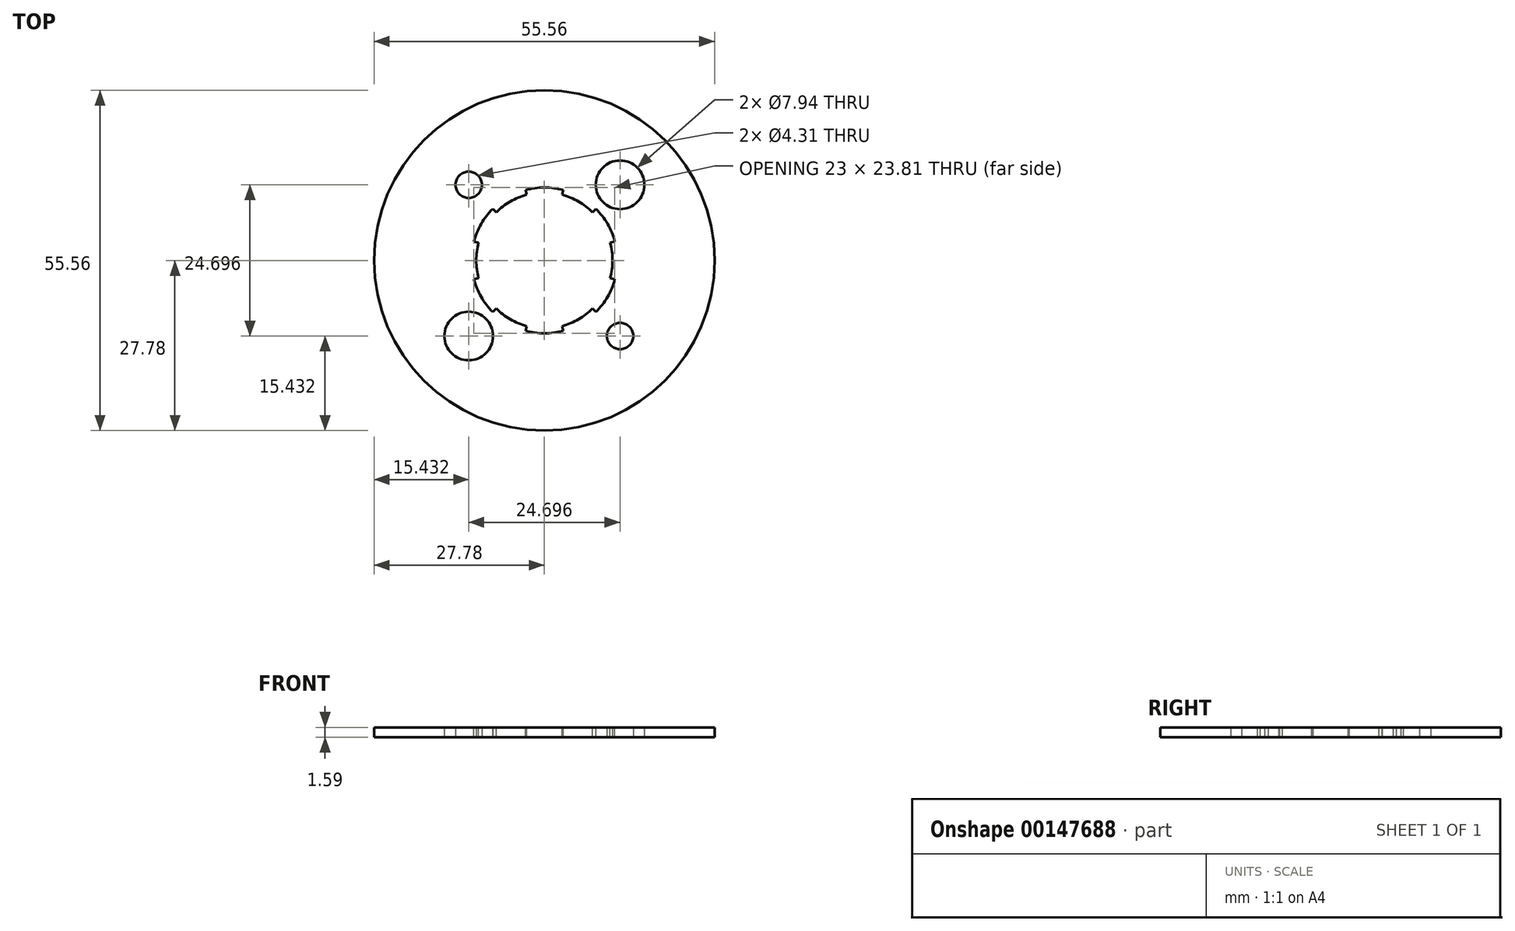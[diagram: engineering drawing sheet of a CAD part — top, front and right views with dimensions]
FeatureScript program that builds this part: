
annotation { "Feature Type Name" : "Feature", "Feature Type Description" : "" }
export const myFeature = defineFeature(function(context is Context, id is Id, definition is map)
    precondition{}
    {
        {
            var Q0;
            Q0=qCreatedBy(makeId("Top.planeOp"),FACE);
            var sketch = newSketch(context, id + "F0", { "sketchPlane" : qUnion([Q0])});
            skCircle(sketch, "E0", {"center": v(0, 0) * mm, "radius": 27.78 * mm});
            skCircle(sketch, "E1", {"center": v(0, 0) * mm, "radius": 11.9 * mm, "construction": true});
            skLineSegment(sketch, "E2.bottom", {"start": v(-12.35, 12.35) * mm, "end": v(12.35, 12.35) * mm, "construction": true});
            skLineSegment(sketch, "E2.top", {"start": v(-12.35, -12.35) * mm, "end": v(12.35, -12.35) * mm, "construction": true});
            skLineSegment(sketch, "E2.left", {"start": v(-12.35, 12.35) * mm, "end": v(-12.35, -12.35) * mm, "construction": true});
            skLineSegment(sketch, "E2.right", {"start": v(12.35, 12.35) * mm, "end": v(12.35, -12.35) * mm, "construction": true});
            skCircle(sketch, "E3", {"center": v(-12.35, 12.35) * mm, "radius": 5.56 * mm, "construction": true});
            skCircle(sketch, "E4", {"center": v(12.35, 12.35) * mm, "radius": 3.97 * mm});
            skCircle(sketch, "E5", {"center": v(-12.35, 12.35) * mm, "radius": 2.15 * mm});
            skCircle(sketch, "E6", {"center": v(-12.35, -12.35) * mm, "radius": 3.97 * mm});
            skCircle(sketch, "E7", {"center": v(12.35, -12.35) * mm, "radius": 2.15 * mm});
            skCircle(sketch, "E8", {"center": v(0, 0) * mm, "radius": 11.11 * mm});
            skSolve(sketch);
        }
        {
            var Q0;
            Q0=qSketchRegion(id+"F0",true);
            extrude(context, id + "F1", {"entities" : qUnion([Q0]), "depth" : 1.59 * mm});
        }
        {
            var Q0;
            Q0=makeQuery(id+"F1.opExtrude","CAP_FACE",FACE,{"disambiguationData":[OSD([sQuery(id+"F0.wireOp",EDGE,"E0"),sQuery(id+"F0.wireOp",EDGE,"E4"),sQuery(id+"F0.wireOp",EDGE,"E5"),sQuery(id+"F0.wireOp",EDGE,"E6"),sQuery(id+"F0.wireOp",EDGE,"E7"),sQuery(id+"F0.wireOp",EDGE,"E8")])],"isStart":false});
            var sketch = newSketch(context, id + "F2", { "sketchPlane" : qUnion([Q0])});
            skLineSegment(sketch, "E9", {"start": v(0, 0) * mm, "end": v(0, 11.11) * mm, "construction": true});
            skLineSegment(sketch, "E10", {"start": v(0, 0) * mm, "end": v(-2.88, 10.73) * mm, "construction": true});
            skLineSegment(sketch, "E11", {"start": v(0, 0) * mm, "end": v(2.88, 10.73) * mm, "construction": true});
            skLineSegment(sketch, "E12", {"start": v(-2.88, 10.73) * mm, "end": v(-3.08, 11.5) * mm});
            skLineSegment(sketch, "E13", {"start": v(2.88, 10.73) * mm, "end": v(3.08, 11.5) * mm});
            skArc(sketch, "E14", {"start": v(2.88, 10.73) * mm, "mid": v(0, 11.11) * mm, "end": v(-2.88, 10.73) * mm});
            skArc(sketch, "E15", {"start": v(3.08, 11.5) * mm, "mid": v(0, 11.9) * mm, "end": v(-3.08, 11.5) * mm});
            skSolve(sketch);
        }
        {
            var Q0;
            Q0=qSketchRegion(id+"F2",true);
            var Q1;
            Q1=makeQuery(id+"F1.opExtrude","CAP_FACE",FACE,{"disambiguationData":[OSD([sQuery(id+"F0.wireOp",EDGE,"E0"),sQuery(id+"F0.wireOp",EDGE,"E4"),sQuery(id+"F0.wireOp",EDGE,"E5"),sQuery(id+"F0.wireOp",EDGE,"E6"),sQuery(id+"F0.wireOp",EDGE,"E7"),sQuery(id+"F0.wireOp",EDGE,"E8")])],"isStart":true});
            extrude(context, id + "F3", {"entities" : qUnion([Q0]), "operationType" : NewBodyOperationType.REMOVE, "endBound" : BoundingType.UP_TO_SURFACE, "oppositeDirection" : true, "endBoundEntityFace" : qUnion([Q1]), "depth" : 25.4 * mm});
        }
        {
            var Q0;
            Q0=makeQuery(id+"F3.boolean.opBoolean","COPY",FACE,{"derivedFrom":makeQuery(id+"F3.opExtrude","SWEPT_FACE",FACE,{"disambiguationData":[OSD([sQuery(id+"F2.wireOp",EDGE,"E12")])]})});
            var Q1;
            Q1=makeQuery(id+"F3.boolean.opBoolean","COPY",FACE,{"derivedFrom":makeQuery(id+"F3.opExtrude","SWEPT_FACE",FACE,{"disambiguationData":[OSD([sQuery(id+"F2.wireOp",EDGE,"E15")])]})});
            var Q2;
            Q2=makeQuery(id+"F3.boolean.opBoolean","COPY",FACE,{"derivedFrom":makeQuery(id+"F3.opExtrude","SWEPT_FACE",FACE,{"disambiguationData":[OSD([sQuery(id+"F2.wireOp",EDGE,"E13")])]})});
            var Q3;
            Q3=makeQuery(id+"F1.opExtrude","SWEPT_FACE",FACE,{"disambiguationData":[OSD([sQuery(id+"F0.wireOp",EDGE,"E8")])]});
            circularPattern(context, id + "F4", {"patternType" : PatternType.FACE, "faces" : qUnion([Q0, Q1, Q2]), "axis" : qUnion([Q3]), "angle" : 60 * degree, "instanceCount" : 6});
        }
    });
